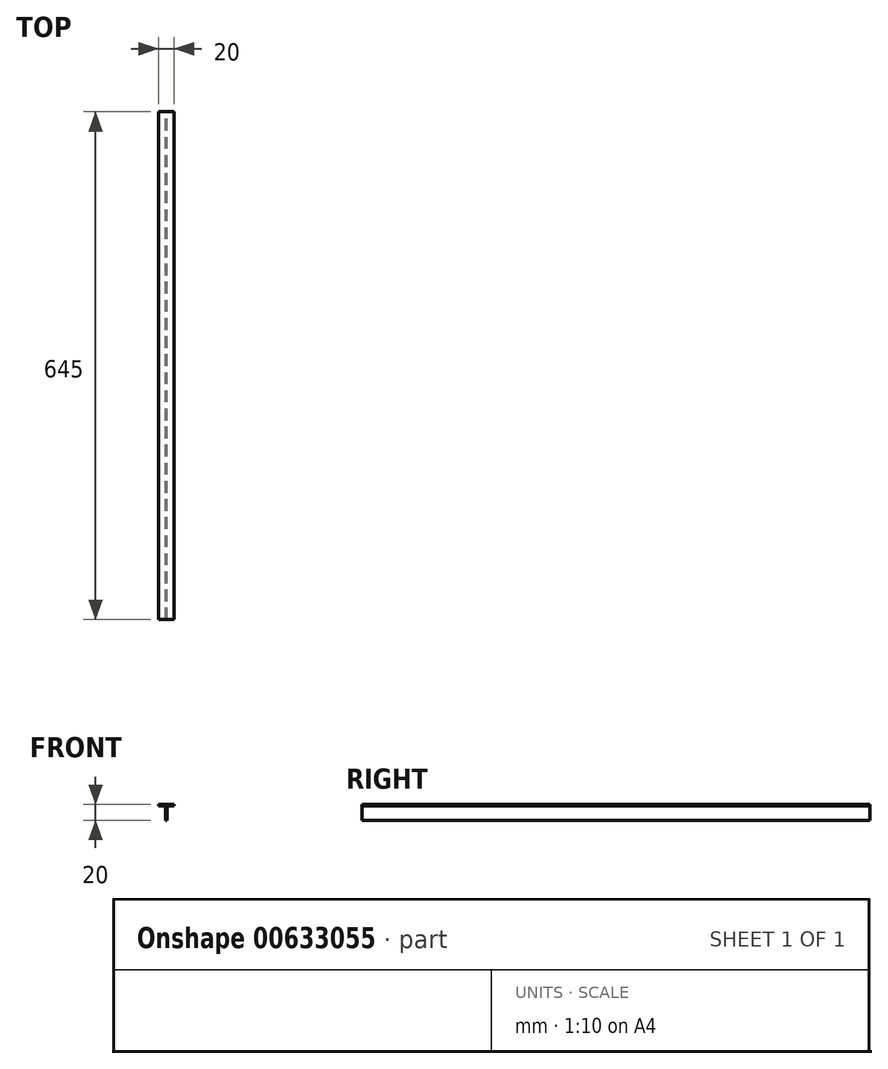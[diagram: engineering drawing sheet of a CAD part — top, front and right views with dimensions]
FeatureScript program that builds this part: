
annotation { "Feature Type Name" : "Feature", "Feature Type Description" : "" }
export const myFeature = defineFeature(function(context is Context, id is Id, definition is map)
    precondition{}
    {
        {
            var Q0;
            Q0=qCreatedBy(makeId("Front.planeOp"),FACE);
            var sketch = newSketch(context, id + "F0", { "sketchPlane" : qUnion([Q0])});
            skLineSegment(sketch, "E0", {"start": v(0, 0) * mm, "end": v(10, 0) * mm});
            skLineSegment(sketch, "E1", {"start": v(10, 0) * mm, "end": v(10, -1.5) * mm});
            skLineSegment(sketch, "E2", {"start": v(10, -1.5) * mm, "end": v(0.75, -1.5) * mm});
            skLineSegment(sketch, "E3", {"start": v(0.75, -1.5) * mm, "end": v(0.75, -20) * mm});
            skLineSegment(sketch, "E4", {"start": v(0.75, -20) * mm, "end": v(0, -20) * mm});
            skLineSegment(sketch, "E5.MirrorCS", {"start": v(0, 0) * mm, "end": v(-10, 0) * mm});
            skLineSegment(sketch, "E6.MirrorCS", {"start": v(-10, 0) * mm, "end": v(-10, -1.5) * mm});
            skLineSegment(sketch, "E7.MirrorCS", {"start": v(-10, -1.5) * mm, "end": v(-0.75, -1.5) * mm});
            skLineSegment(sketch, "E8.MirrorCS", {"start": v(-0.75, -1.5) * mm, "end": v(-0.75, -20) * mm});
            skLineSegment(sketch, "E9.MirrorCS", {"start": v(-0.75, -20) * mm, "end": v(0, -20) * mm});
            skSolve(sketch);
        }
        {
            var Q0;
            Q0=makeQuery(id+"F0.imprint","IMPRINT",FACE,{"disambiguationData":[TD([[makeQuery(id+"F0.imprint","IMPRINT",EDGE,{"derivedFrom":sQuery(id+"F0.wireOp",EDGE,"E0")}),-1.0]])]});
            extrude(context, id + "F1", {"entities" : qUnion([Q0]), "depth" : 610 * mm + 35 * mm, "offsetDistance" : 25 * mm});
        }
    });
